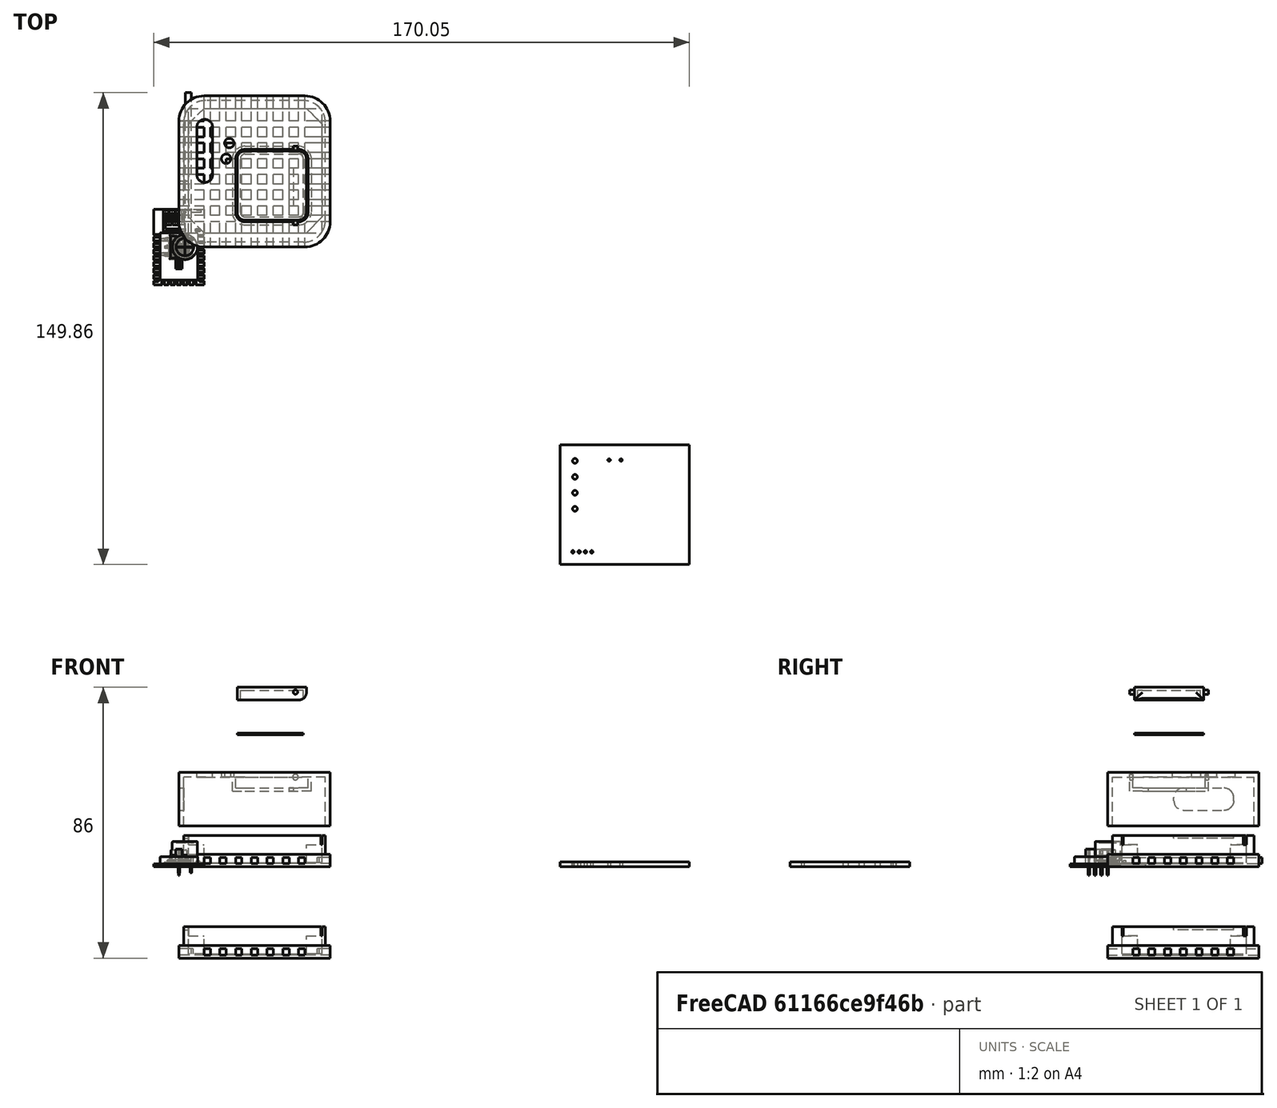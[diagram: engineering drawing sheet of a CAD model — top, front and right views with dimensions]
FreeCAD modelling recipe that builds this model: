
FCSTD DOCUMENT  (FreeCAD 1.0R39109 (Git))
Label: box_rs
License: All rights reserved
LicenseURL: http://en.wikipedia.org/wiki/All_rights_reserved
objects: Part::Feature×28, App::Part×28, Part::Box×19, Part::Cut×18, Part::Fillet×16, Part::Cylinder×6, Part::Chamfer×2, Part::MultiFuse×2, Part::FeaturePython×2, Part::MultiCommon×1
note: 92 computed .brp shape members not serialized (recipe doc carries the construction recipe); baked Part::Feature solids carry a one-line shape summary decoded from their .brp

FEATURE [Part::Feature] Part__Feature  label="R_0805_2012Metric"
  shape: bbox 2 x 1.2 x 0.45 mm, 26 faces (baked)
FEATURE [App::Part] R_0805_2012Metric  label="R_0805_2012Metric001"
  Group = -> [Part__Feature]
  Origin = -> Origin
  Placement = pos=(156.339,-86.614,1.65) rot=(0,0,1;0rad)
FEATURE [Part::Feature] Part__Feature001  label="PinSocket_1x04_P2.00mm_Vertical"
  shape: bbox 2 x 8 x 8.3 mm, 114 faces (baked)
FEATURE [App::Part] PinSocket_1x04_P2_00mm_Vertical  label="PinSocket_1x04_P2.00mm_Vertical001"
  Group = -> [Part__Feature001]
  Origin = -> Origin001
  Placement = pos=(131.083,-96.8248,1.65) rot=(0,0,-1;1.5708rad)
FEATURE [Part::Feature] Part__Feature002  label="LED_1206_3216Metric"
  shape: bbox 3.2 x 1.6 x 1.1 mm, 50 faces (baked)
FEATURE [App::Part] LED_1206_3216Metric  label="LED_1206_3216Metric001"
  Group = -> [Part__Feature002]
  Origin = -> Origin002
  Placement = pos=(133.502,-72.9488,1.65) rot=(0,0,1;3.14159rad)
FEATURE [Part::Feature] Part__Feature003  label="CP_Radial_D80mm_P380mm"
  shape: bbox 9.886 x 10.23 x 10 mm, 54 faces (baked)
FEATURE [App::Part] CP_Radial_D8_0mm_P3_80mm  label="CP_Radial_D8.0mm_P3.80mm"
  Group = -> [Part__Feature003]
  Origin = -> Origin003
  Placement = pos=(140.386,-67.6656,1.65) rot=(0,0,1;3.14159rad)
FEATURE [Part::Feature] Part__Feature004  label="ESP_12E001_cp"
  shape: bbox 16 x 24 x 3.2 mm, 488 faces, 48 solids (baked)
FEATURE [App::Part] ESP_12E  label="ESP-12E"
  Group = -> [Part__Feature004]
  Origin = -> Origin004
  Placement = pos=(145.079,-87.1526,1.65) rot=(0,0,1;3.14159rad)
FEATURE [Part::Feature] Part__Feature005  label="LED_1206_3216Metric002"
  shape: bbox 3.2 x 1.6 x 1.1 mm, 50 faces (baked)
FEATURE [App::Part] LED_1206_3216Metric001  label="LED_1206_3216Metric003"
  Group = -> [Part__Feature005]
  Origin = -> Origin005
  Placement = pos=(132.537,-77.9272,1.65) rot=(0,0,-1;1.5708rad)
FEATURE [Part::Feature] Part__Feature006  label="R_0805_2012Metric002"
  shape: bbox 2 x 1.2 x 0.45 mm, 26 faces (baked)
FEATURE [App::Part] R_0805_2012Metric001  label="R_0805_2012Metric003"
  Group = -> [Part__Feature006]
  Origin = -> Origin006
  Placement = pos=(133.631,-83.0834,1.65) rot=(0,0,1;3.14159rad)
FEATURE [Part::Feature] Part__Feature007  label="R_0805_2012Metric004"
  shape: bbox 2 x 1.2 x 0.45 mm, 26 faces (baked)
FEATURE [App::Part] R_0805_2012Metric002  label="R_0805_2012Metric005"
  Group = -> [Part__Feature007]
  Origin = -> Origin007
  Placement = pos=(137.869,-72.898,1.65) rot=(0,0,1;0rad)
FEATURE [Part::Feature] Part__Feature008  label="R_0805_2012Metric006"
  shape: bbox 2 x 1.2 x 0.45 mm, 26 faces (baked)
FEATURE [App::Part] R_0805_2012Metric003  label="R_0805_2012Metric007"
  Group = -> [Part__Feature008]
  Origin = -> Origin008
  Placement = pos=(134.849,-77.6732,1.65) rot=(0,0,1;1.5708rad)
FEATURE [Part::Feature] Part__Feature009  label="R_1206_3216Metric"
  shape: bbox 3.2 x 1.6 x 0.55 mm, 26 faces (baked)
FEATURE [App::Part] R_1206_3216Metric  label="R_1206_3216Metric001"
  Group = -> [Part__Feature009]
  Origin = -> Origin009
  Placement = pos=(127.914,-91.059,-0.05) rot=(0,1,0;3.14159rad)
FEATURE [Part::Feature] Part__Feature010  label="DIP_6_W762mm_SMDSocket"
  shape: bbox 8.952 x 7.74 x 3.68 mm, 116 faces (baked)
FEATURE [App::Part] DIP_6_W7_62mm_SMDSocket  label="DIP-6_W7.62mm_SMDSocket"
  Group = -> [Part__Feature010]
  Origin = -> Origin010
  Placement = pos=(137.439,-80.5434,-0.05) rot=(0,1,0;3.14159rad)
FEATURE [Part::Feature] Part__Feature011  label="C_1206_3216Metric"
  shape: bbox 3.2 x 1.6 x 1.6 mm, 28 faces (baked)
FEATURE [App::Part] C_1206_3216Metric  label="C_1206_3216Metric001"
  Group = -> [Part__Feature011]
  Origin = -> Origin011
  Placement = pos=(125.247,-88.2904,-0.05) rot=(0,1,0;3.14159rad)
FEATURE [Part::Feature] Part__Feature012  label="CQ assembly"
  shape: bbox 9.9 x 6.5 x 2.32 mm, 83 faces, 5 solids (baked)
FEATURE [App::Part] TO_252_2  label="TO-252-2"
  Group = -> [Part__Feature012]
  Origin = -> Origin012
  Placement = pos=(136.324,-91.2405,-0.05) rot=(1,0,0;3.14159rad)
FEATURE [Part::Feature] Part__Feature013  label="R_0805_2012Metric008"
  shape: bbox 2 x 1.2 x 0.45 mm, 26 faces (baked)
FEATURE [App::Part] R_0805_2012Metric004  label="R_0805_2012Metric009"
  Group = -> [Part__Feature013]
  Origin = -> Origin013
  Placement = pos=(134.47,-86.3854,-0.05) rot=(0,1,0;3.14159rad)
FEATURE [Part::Feature] Part__Feature014  label="D_MELF_Standard"
  shape: bbox 5.8 x 2.2 x 2.2 mm, 13 faces (baked)
FEATURE [App::Part] D_MELF
  Group = -> [Part__Feature014]
  Origin = -> Origin014
  Placement = pos=(140.767,-72.9488,-0.05) rot=(0.707107,-0.707107,0;3.14159rad)
FEATURE [Part::Feature] Part__Feature015  label="R_0805_2012Metric010"
  shape: bbox 2 x 1.2 x 0.45 mm, 26 faces (baked)
FEATURE [App::Part] R_0805_2012Metric005  label="R_0805_2012Metric011"
  Group = -> [Part__Feature015]
  Origin = -> Origin015
  Placement = pos=(145.188,-78.7654,-0.05) rot=(1,0,0;3.14159rad)
FEATURE [Part::Feature] Part__Feature016  label="CP_Elec_5x54"
  shape: bbox 6.985 x 6.828 x 5.4 mm, 41 faces (baked)
FEATURE [App::Part] CP_Elec_5x5_4  label="CP_Elec_5x5.4"
  Group = -> [Part__Feature016]
  Origin = -> Origin016
  Placement = pos=(145.898,-85.979,-0.05) rot=(0,1,0;3.14159rad)
FEATURE [Part::Feature] Part__Feature017  label="R_0805_2012Metric012"
  shape: bbox 2 x 1.2 x 0.45 mm, 26 faces (baked)
FEATURE [App::Part] R_0805_2012Metric006  label="R_0805_2012Metric013"
  Group = -> [Part__Feature017]
  Origin = -> Origin017
  Placement = pos=(145.137,-81.8642,-0.05) rot=(0,1,0;3.14159rad)
FEATURE [Part::Feature] Part__Feature018  label="R_1206_3216Metric002"
  shape: bbox 3.2 x 1.6 x 0.55 mm, 26 faces (baked)
FEATURE [App::Part] R_1206_3216Metric001  label="R_1206_3216Metric003"
  Group = -> [Part__Feature018]
  Origin = -> Origin018
  Placement = pos=(130.937,-77.8764,-0.05) rot=(0.707107,0.707107,0;3.14159rad)
FEATURE [Part::Feature] Part__Feature019  label="CP_Elec_5x055"
  shape: bbox 6.985 x 6.828 x 5.4 mm, 41 faces (baked)
FEATURE [App::Part] CP_Elec_5x5_005  label="CP_Elec_5x5.005"
  Group = -> [Part__Feature019]
  Origin = -> Origin019
  Placement = pos=(150.749,-78.1304,-0.05) rot=(0.707107,-0.707107,0;3.14159rad)
FEATURE [Part::Feature] Part__Feature020  label="R_0805_2012Metric014"
  shape: bbox 2 x 1.2 x 0.45 mm, 26 faces (baked)
FEATURE [App::Part] R_0805_2012Metric007  label="R_0805_2012Metric015"
  Group = -> [Part__Feature020]
  Origin = -> Origin020
  Placement = pos=(152.908,-71.374,-0.05) rot=(1,0,0;3.14159rad)
FEATURE [Part::Feature] Part__Feature021  label="C_1206_3216Metric002"
  shape: bbox 3.2 x 1.6 x 1.6 mm, 28 faces (baked)
FEATURE [App::Part] C_1206_3216Metric001  label="C_1206_3216Metric003"
  Group = -> [Part__Feature021]
  Origin = -> Origin021
  Placement = pos=(145.339,-75.5142,-0.05) rot=(0,1,0;3.14159rad)
FEATURE [Part::Feature] Part__Feature022  label="TO-269AA"
  shape: bbox 6.5 x 4.7 x 1.625 mm, 54 faces (baked)
FEATURE [App::Part] TO_269AA  label="TO-269AA001"
  Group = -> [Part__Feature022]
  Origin = -> Origin022
  Placement = pos=(134.442,-72.0344,-0.05) rot=(1,0,0;3.14159rad)
FEATURE [Part::Feature] Part__Feature023  label="R_0805_2012Metric016"
  shape: bbox 2 x 1.2 x 0.45 mm, 26 faces (baked)
FEATURE [App::Part] R_0805_2012Metric008  label="R_0805_2012Metric017"
  Group = -> [Part__Feature023]
  Origin = -> Origin023
  Placement = pos=(152.908,-69.088,-0.05) rot=(1,0,0;3.14159rad)
FEATURE [Part::Feature] Part__Feature024  label="R_1206_3216Metric004"
  shape: bbox 3.2 x 1.6 x 0.55 mm, 26 faces (baked)
FEATURE [App::Part] R_1206_3216Metric002  label="R_1206_3216Metric005"
  Group = -> [Part__Feature024]
  Origin = -> Origin024
  Placement = pos=(132.142,-67.1576,-0.05) rot=(1,0,0;3.14159rad)
FEATURE [Part::Feature] Part__Feature025  label="PowerIntegrations_SO_8C"
  shape: bbox 6 x 4.9 x 1.6 mm, 141 faces (baked)
FEATURE [App::Part] PowerIntegrations_SO_8C  label="PowerIntegrations_SO-8C"
  Group = -> [Part__Feature025]
  Origin = -> Origin025
  Placement = pos=(147.041,-70.9359,-0.05) rot=(1,0,0;3.14159rad)
FEATURE [Part::Feature] Part__Feature026  label="D_MELF_Standard001"
  shape: bbox 5.8 x 2.2 x 2.2 mm, 13 faces (baked)
FEATURE [App::Part] D_MELF001
  Group = -> [Part__Feature026]
  Origin = -> Origin026
  Placement = pos=(157.607,-67.831,-0.05) rot=(0.707107,0.707107,0;3.14159rad)
FEATURE [Part::Feature] Part__Feature027  label="RS_Board_PCB"
  shape: bbox 41 x 38 x 1.6 mm, 16 faces (baked)
FEATURE [App::Part] RS_Board_1  label="RS_Board 1"
  Group = -> [R_0805_2012Metric,PinSocket_1x04_P2_00mm_Vertical,LED_1206_3216Metric,CP_Radial_D8_0mm_P3_80mm,ESP_12E,LED_1206_3216Metric001,R_0805_2012Metric001,R_0805_2012Metric002,R_0805_2012Metric003,R_1206_3216Metric,DIP_6_W7_62mm_SMDSocket,C_1206_3216Metric,TO_252_2,R_0805_2012Metric004,D_MELF,R_0805_2012Metric005,CP_Elec_5x5_4,R_0805_2012Metric006,R_1206_3216Metric001,CP_Elec_5x5_005,R_0805_2012Metric007,+7 more]
  Origin = -> Origin027
  Placement = pos=(-117.5,106,-8) rot=(0,0,1;0rad)
FEATURE [Part::Box] Box  label="Куб"
  AttacherType = Attacher::AttachEngine3D
  Height = 10
  Length = 48
  Width = 48
FEATURE [Part::Box] Box001  label="Куб001"
  AttacherType = Attacher::AttachEngine3D
  Height = 10
  Length = 42.5
  Placement = pos=(3,4.5,0) rot=(0,0,1;0rad)
  Width = 39.5
FEATURE [Part::Box] Box002  label="Куб002"
  AttacherType = Attacher::AttachEngine3D
  Height = 3
  Length = 42.5
  Placement = pos=(3,4.5,7) rot=(0,0,1;0rad)
  Width = 39.5
FEATURE [Part::Chamfer] Chamfer
  Base = -> Box001
  EdgeLinks = -> Box001 [Edge5]
  Edges = 1 edges r=5: [Edge5]
FEATURE [Part::Chamfer] Chamfer001
  Base = -> Chamfer
  EdgeLinks = -> Chamfer [Edge3,Edge12,Edge15]
  Edges = 3 edges r=5: [Edge3,Edge12,Edge15]
  Placement = pos=(0,0,1.3) rot=(0,0,1;0rad)
FEATURE [Part::Cut] Cut
  Base = -> Box
  Tool = -> Box002
FEATURE [Part::Cut] Cut001
  Base = -> Cut
  Tool = -> Chamfer001
FEATURE [Part::Fillet] Fillet
  Base = -> Cut001
  EdgeLinks = -> Cut001 [Edge1,Edge3,Edge6,Edge23]
  Edges = 4 edges r=8: [Edge1,Edge3,Edge6,Edge23]
FEATURE [Part::Box] Box003  label="Куб003"
  AttacherType = Attacher::AttachEngine3D
  Height = 17
  Length = 48
  Placement = pos=(0,0,4) rot=(0,0,1;0rad)
  Width = 48
FEATURE [Part::Fillet] Fillet001
  Base = -> Box003
  EdgeLinks = -> Box003 [Edge1,Edge3,Edge5,Edge7]
  Edges = 4 edges r=8: [Edge1,Edge3,Edge5,Edge7]
FEATURE [Part::Box] Box004  label="Куб004"
  AttacherType = Attacher::AttachEngine3D
  Height = 17
  Length = 45
  Placement = pos=(1.5,1.5,4) rot=(0,0,1;0rad)
  Width = 45
FEATURE [Part::Fillet] Fillet002
  Base = -> Box004
  EdgeLinks = -> Box004 [Edge5]
  Edges = 1 edges r=7: [Edge5]
FEATURE [Part::Fillet] Fillet003
  Base = -> Fillet002
  EdgeLinks = -> Fillet002 [Edge3,Edge12,Edge15]
  Edges = 3 edges r=7: [Edge3,Edge12,Edge15]
  Placement = pos=(0,0,-1.5) rot=(0,0,1;0rad)
FEATURE [Part::Cut] Cut002
  Base = -> Fillet001
  Tool = -> Fillet003
FEATURE [Part::Box] Box005  label="Куб005"
  AttacherType = Attacher::AttachEngine3D
  Height = 17
  Length = 48
  Placement = pos=(0,0,4) rot=(0,0,1;0rad)
  Width = 48
FEATURE [Part::Box] Box006  label="Куб006"
  AttacherType = Attacher::AttachEngine3D
  Height = 17
  Length = 45
  Placement = pos=(1.5,1.5,4) rot=(0,0,1;0rad)
  Width = 45
FEATURE [Part::Fillet] Fillet004
  Base = -> Box005
  EdgeLinks = -> Box005 [Edge1,Edge3,Edge5,Edge7]
  Edges = 4 edges r=8: [Edge1,Edge3,Edge5,Edge7]
FEATURE [Part::Fillet] Fillet005
  Base = -> Box006
  EdgeLinks = -> Box006 [Edge5]
  Edges = 1 edges r=7: [Edge5]
FEATURE [Part::Fillet] Fillet006
  Base = -> Fillet005
  EdgeLinks = -> Fillet005 [Edge3,Edge12,Edge15]
  Edges = 3 edges r=7: [Edge3,Edge12,Edge15]
  Placement = pos=(0,0,-1.5) rot=(0,0,1;0rad)
FEATURE [Part::Cut] Cut003
  Base = -> Fillet004
  Tool = -> Fillet006
FEATURE [Part::Cut] Cut004
  Base = -> Fillet
  Tool = -> Cut002
FEATURE [Part::Box] Box007  label="Куб007"
  AttacherType = Attacher::AttachEngine3D
  Height = 7
  Length = 5
  Placement = pos=(0,21,9) rot=(0,0,1;0rad)
  Width = 19
FEATURE [Part::Box] Box008  label="Куб008"
  AttacherType = Attacher::AttachEngine3D
  Height = 7
  Length = 5
  Placement = pos=(0,21,9) rot=(0,0,1;0rad)
  Width = 19
FEATURE [Part::Cut] Cut005
  Base = -> Cut004
  Tool = -> Box007
FEATURE [Part::Fillet] Fillet007
  Base = -> Box008
  EdgeLinks = -> Box008 [Edge11,Edge12]
  Edges = 2 edges r=3: [Edge11,Edge12]
FEATURE [Part::Fillet] Fillet008
  Base = -> Fillet007
  EdgeLinks = -> Fillet007 [Edge8,Edge12]
  Edges = 2 edges r=3: [Edge8,Edge12]
FEATURE [Part::Cut] Cut006
  Base = -> Cut003
  Tool = -> Fillet008
FEATURE [Part::Box] Box009  label="Куб009"
  AttacherType = Attacher::AttachEngine3D
  Height = 5
  Length = 5
  Placement = pos=(5.7,20.5,17) rot=(0,0,1;0rad)
  Width = 20
FEATURE [Part::Fillet] Fillet009
  Base = -> Box009
  EdgeLinks = -> Box009 [Edge1,Edge3,Edge5,Edge7]
  Edges = 4 edges r=2.4: [Edge1,Edge3,Edge5,Edge7]
FEATURE [Part::Cut] Cut007
  Base = -> Cut006
  Tool = -> Fillet009
FEATURE [Part::Cylinder] Cylinder  label="Цилиндр"
  Angle = 360
  AttacherType = Attacher::AttachEngine3D
  FirstAngle = 0
  Height = 10
  Placement = pos=(15,28,16) rot=(0,0,1;0rad)
  Radius = 1.5
  SecondAngle = 0
FEATURE [Part::Cylinder] Cylinder001  label="Цилиндр001"
  Angle = 360
  AttacherType = Attacher::AttachEngine3D
  FirstAngle = 0
  Height = 10
  Placement = pos=(16,33,16) rot=(0,0,1;0rad)
  Radius = 1.5
  SecondAngle = 0
FEATURE [Part::Cut] Cut008
  Base = -> Cut007
  Tool = -> Cylinder
FEATURE [Part::Cut] Cut009
  Base = -> Cut008
  Tool = -> Cylinder001
FEATURE [Part::Box] Box010  label="Куб010"
  AttacherType = Attacher::AttachEngine3D
  Height = 6
  Length = 25
  Placement = pos=(17,7,15) rot=(0,0,1;0rad)
  Width = 25
FEATURE [Part::Box] Box011  label="Куб011"
  AttacherType = Attacher::AttachEngine3D
  Height = 3
  Length = 20
  Placement = pos=(19.5,9.5,21) rot=(0,0,1;0rad)
  Width = 20
FEATURE [Part::Fillet] Fillet010
  Base = -> Box011
  EdgeLinks = -> Box011 [Edge1,Edge3,Edge5,Edge7]
  Edges = 4 edges r=1.5: [Edge1,Edge3,Edge5,Edge7]
  Placement = pos=(0,0,-4) rot=(0,0,1;0rad)
FEATURE [Part::Box] Box012  label="Куб012"
  AttacherType = Attacher::AttachEngine3D
  Height = 6
  Length = 23
  Placement = pos=(18,8,15) rot=(0,0,1;0rad)
  Width = 23
FEATURE [Part::Fillet] Fillet011
  Base = -> Box012
  EdgeLinks = -> Box012 [Edge1,Edge3,Edge5,Edge7]
  Edges = 4 edges r=3: [Edge1,Edge3,Edge5,Edge7]
  Placement = pos=(0,0,1) rot=(0,0,1;0rad)
FEATURE [Part::Fillet] Fillet012
  Base = -> Box010
  EdgeLinks = -> Box010 [Edge1,Edge3,Edge5,Edge7]
  Edges = 4 edges r=4: [Edge1,Edge3,Edge5,Edge7]
FEATURE [Part::MultiFuse] Fusion
  Shapes = -> [Fillet012,Cut009]
FEATURE [Part::Cut] Cut010
  Base = -> Fusion
  Tool = -> Fillet011
FEATURE [Part::Box] Box013  label="Куб013"
  AttacherType = Attacher::AttachEngine3D
  Height = 4
  Length = 22
  Placement = pos=(18.5,8.5,17) rot=(0,0,1;0rad)
  Width = 22
FEATURE [Part::Fillet] Fillet013
  Base = -> Box013
  EdgeLinks = -> Box013 [Edge1,Edge3,Edge5,Edge7]
  Edges = 4 edges r=2.5: [Edge1,Edge3,Edge5,Edge7]
FEATURE [Part::Cut] Cut011
  Base = -> Fillet013
  Tool = -> Fillet010
FEATURE [Part::Cylinder] Cylinder002  label="Цилиндр002"
  Angle = 360
  AttacherType = Attacher::AttachEngine3D
  FirstAngle = 0
  Height = 2
  Placement = pos=(37,9,19.5) rot=(1,0,0;1.5708rad)
  Radius = 0.7
  SecondAngle = 0
FEATURE [Part::Cylinder] Cylinder003  label="Цилиндр003"
  Angle = 360
  AttacherType = Attacher::AttachEngine3D
  FirstAngle = 0
  Height = 2
  Placement = pos=(37,32,19.5) rot=(1,0,0;1.5708rad)
  Radius = 0.7
  SecondAngle = 0
FEATURE [Part::Cylinder] Cylinder004  label="Цилиндр004"
  Angle = 360
  AttacherType = Attacher::AttachEngine3D
  FirstAngle = 0
  Height = 2
  Placement = pos=(37,9,19.5) rot=(1,0,0;1.5708rad)
  Radius = 0.9
  SecondAngle = 0
FEATURE [Part::Cylinder] Cylinder005  label="Цилиндр005"
  Angle = 360
  AttacherType = Attacher::AttachEngine3D
  FirstAngle = 0
  Height = 2
  Placement = pos=(37,32,19.5) rot=(1,0,0;1.5708rad)
  Radius = 0.9
  SecondAngle = 0
FEATURE [Part::MultiFuse] Fusion001
  Shapes = -> [Cut011,Cylinder002,Cylinder003]
FEATURE [Part::Cut] Cut012
  Base = -> Cut010
  Tool = -> Cylinder004
FEATURE [Part::Cut] Cut013
  Base = -> Cut012
  Tool = -> Cylinder005
FEATURE [Part::Box] Box014  label="Куб014"
  AttacherType = Attacher::AttachEngine3D
  Height = 5
  Length = 22
  Placement = pos=(18.5,6.5,17) rot=(0,0,1;0rad)
  Width = 26
FEATURE [Part::Fillet] Fillet014
  Base = -> Box014
  EdgeLinks = -> Box014 [Edge8]
  Edges = 1 edges r=2.4: [Edge8]
FEATURE [Part::MultiCommon] Common
  Placement = pos=(0,0,36) rot=(0,0,1;0rad)
  Shapes = -> [Fusion001,Fillet014]
FEATURE [Part::Box] Box015  label="Куб015"
  AttacherType = Attacher::AttachEngine3D
  Height = 10
  Length = 1.5
  Placement = pos=(35,13,10) rot=(0,0,1;0rad)
  Width = 12
FEATURE [Part::Cut] Cut014
  Base = -> Cut013
  Placement = pos=(0,0,9) rot=(0,0,1;0rad)
  Tool = -> Box015
FEATURE [Part::Box] Box016  label="Куб016"
  AttacherType = Attacher::AttachEngine3D
  Height = 0.5
  Length = 21
  Placement = pos=(18.5,8.5,17) rot=(0,0,1;0rad)
  Width = 22
FEATURE [Part::Fillet] Fillet015
  Base = -> Box016
  EdgeLinks = -> Box016 [Edge1,Edge3,Edge5,Edge7]
  Edges = 4 edges r=2.5: [Edge1,Edge3,Edge5,Edge7]
  Placement = pos=(0,0,25) rot=(0,0,1;0rad)
FEATURE [Part::Box] Box017  label="Куб017"
  AttacherType = Attacher::AttachEngine3D
  Height = 2
  Length = 2
  Placement = pos=(2,0,1) rot=(0,0,1;0rad)
  Width = 49
FEATURE [Part::FeaturePython] Array  # Draft array (typed FeaturePython)
  AlwaysSyncPlacement = false
  Angle = 360
  ArrayType = 0
  Axis = (0,0,1)
  Base = -> Box017
  Center = (0,0,0)
  Count = 7
  ExpandArray = false
  Fuse = false
  IntervalAxis = (0,0,0)
  IntervalX = (5,0,0)
  IntervalY = (0,100,0)
  IntervalZ = (0,0,100)
  NumberCircles = 3
  NumberPolar = 5
  NumberX = 7
  NumberY = 1
  NumberZ = 1
  Placement = pos=(6,-1,0) rot=(0,0,1;0rad)
  PlacementList = 7 placements: arithmetic series from (2,0,1) step (5,0,0) to (32,0,1)
  RadialDistance = 50
  ScaleList = (7) [(1,1,1),(1,1,1),(1,1,1),(1,1,1),(1,1,1),(1,1,1),(1,1,1)]
  Symmetry = 1
  TangentialDistance = 25
FEATURE [Part::Box] Box018  label="Куб018"
  AttacherType = Attacher::AttachEngine3D
  Height = 2
  Length = 2
  Placement = pos=(2,0,1) rot=(0,0,1;0rad)
  Width = 49
FEATURE [Part::FeaturePython] Array001  # Draft array (typed FeaturePython)
  AlwaysSyncPlacement = false
  Angle = 360
  ArrayType = 0
  Axis = (0,0,1)
  Base = -> Box018
  Center = (0,0,0)
  Count = 7
  ExpandArray = false
  Fuse = false
  IntervalAxis = (0,0,0)
  IntervalX = (5,0,0)
  IntervalY = (0,100,0)
  IntervalZ = (0,0,100)
  NumberCircles = 3
  NumberPolar = 5
  NumberX = 7
  NumberY = 1
  NumberZ = 1
  Placement = pos=(49,6,0) rot=(0,0,1;1.5708rad)
  PlacementList = 7 placements: arithmetic series from (2,0,1) step (5,0,0) to (32,0,1)
  RadialDistance = 50
  ScaleList = (7) [(1,1,1),(1,1,1),(1,1,1),(1,1,1),(1,1,1),(1,1,1),(1,1,1)]
  Symmetry = 1
  TangentialDistance = 25
FEATURE [Part::Cut] Cut015
  Base = -> Cut005
  Tool = -> Array
FEATURE [Part::Cut] Cut016
  Base = -> Cut015
  Tool = -> Array001
FEATURE [Part::Cut] Cut017
  Base = -> Cut015
  Placement = pos=(0,0,-29) rot=(0,0,1;0rad)
  Tool = -> Array001
